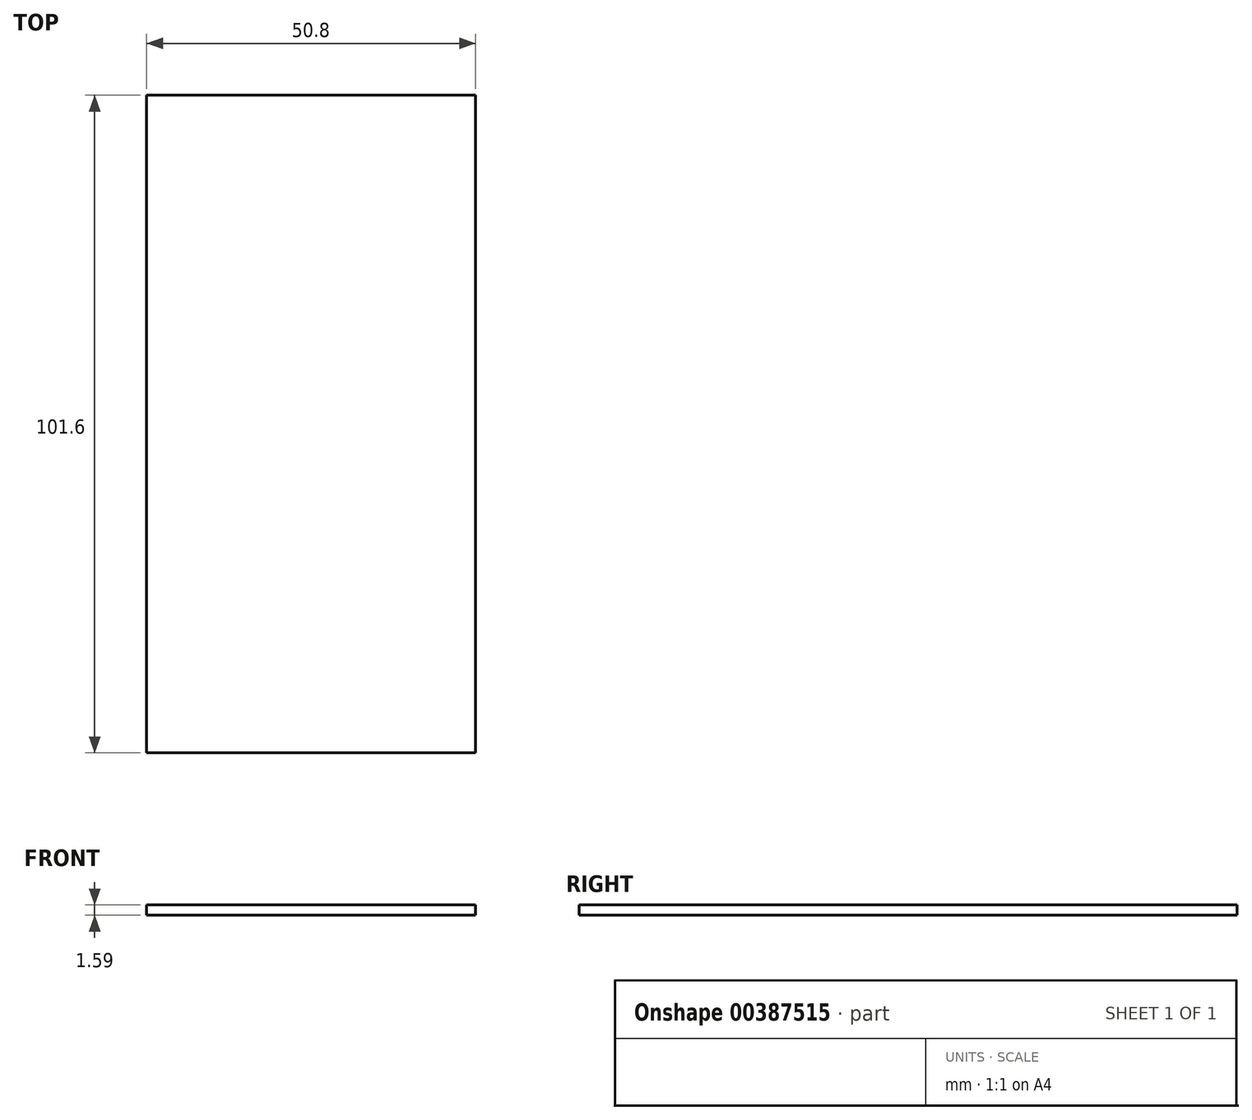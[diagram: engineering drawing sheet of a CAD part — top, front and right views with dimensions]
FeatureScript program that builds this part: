
annotation { "Feature Type Name" : "Feature", "Feature Type Description" : "" }
export const myFeature = defineFeature(function(context is Context, id is Id, definition is map)
    precondition{}
    {
        {
            var Q0;
            Q0=qCreatedBy(makeId("Top.planeOp"),FACE);
            var sketch = newSketch(context, id + "F0", { "sketchPlane" : qUnion([Q0])});
            skLineSegment(sketch, "E0.bottom", {"start": v(0, 0) * mm, "end": v(50.8, 0) * mm});
            skLineSegment(sketch, "E0.top", {"start": v(0, 101.6) * mm, "end": v(50.8, 101.6) * mm});
            skLineSegment(sketch, "E0.left", {"start": v(0, 0) * mm, "end": v(0, 101.6) * mm});
            skLineSegment(sketch, "E0.right", {"start": v(50.8, 0) * mm, "end": v(50.8, 101.6) * mm});
            skSolve(sketch);
        }
        {
            var Q0;
            Q0=makeQuery(id+"F0.imprint","IMPRINT",FACE,{"disambiguationData":[TD([[makeQuery(id+"F0.imprint","IMPRINT",EDGE,{"derivedFrom":sQuery(id+"F0.wireOp",EDGE,"E0.bottom")}),1.0]])]});
            extrude(context, id + "F1", {"entities" : qUnion([Q0]), "depth" : 1.59 * mm});
        }
    });
